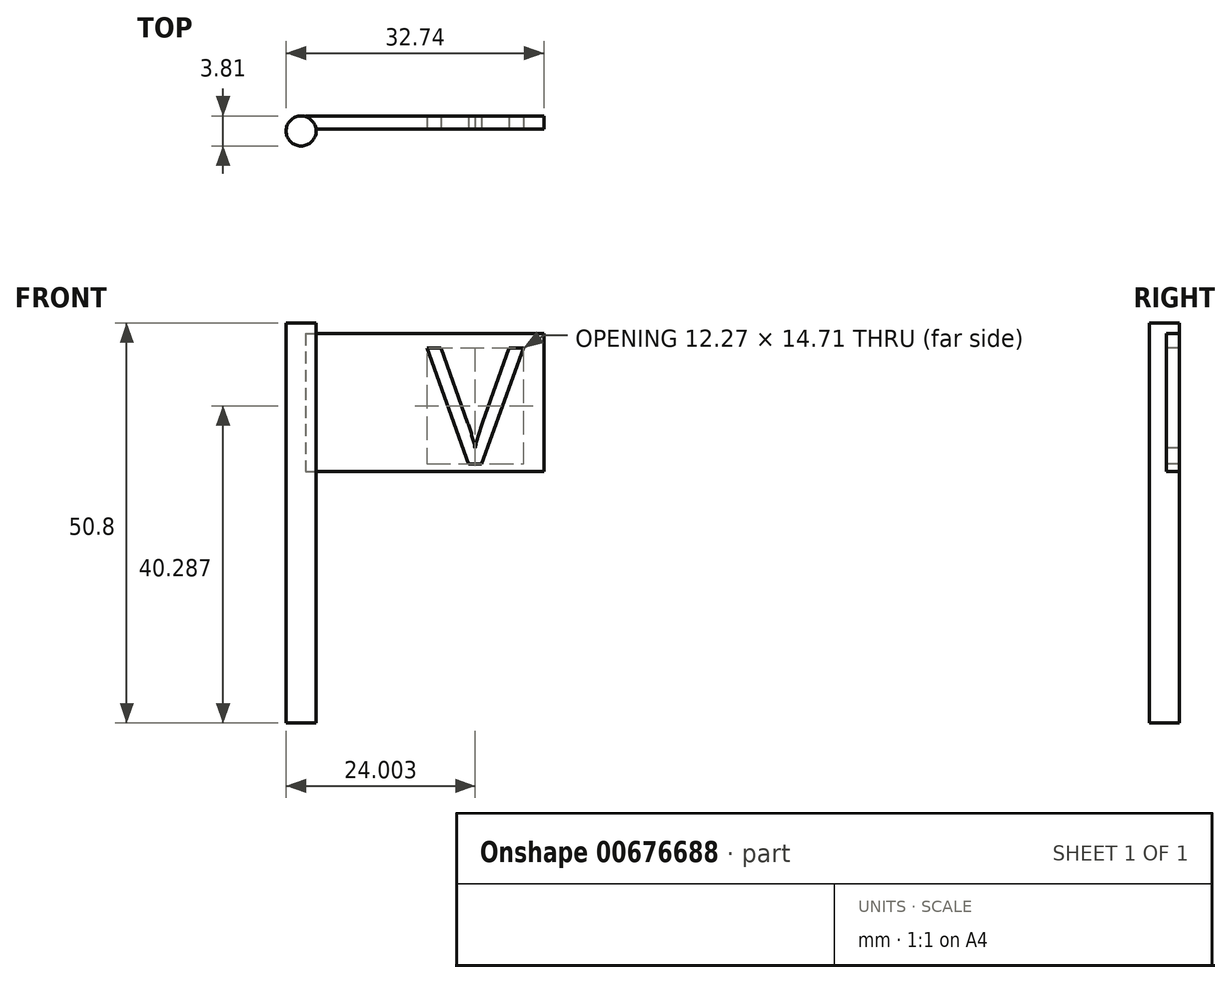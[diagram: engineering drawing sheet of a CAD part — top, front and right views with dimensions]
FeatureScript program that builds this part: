
annotation { "Feature Type Name" : "Feature", "Feature Type Description" : "" }
export const myFeature = defineFeature(function(context is Context, id is Id, definition is map)
    precondition{}
    {
        {
            var Q0;
            Q0=qCreatedBy(makeId("Top.planeOp"),FACE);
            var sketch = newSketch(context, id + "F0", { "sketchPlane" : qUnion([Q0])});
            skCircle(sketch, "E0", {"center": v(-29.57, 21.63) * mm, "radius": 1.9 * mm});
            skSolve(sketch);
        }
        {
            var Q0;
            Q0=makeQuery(id+"F0.imprint","IMPRINT",FACE,{"disambiguationData":[TD([[makeQuery(id+"F0.imprint","IMPRINT",EDGE,{"derivedFrom":sQuery(id+"F0.wireOp",EDGE,"E0")}),1.0]])]});
            extrude(context, id + "F1", {"entities" : qUnion([Q0]), "endBound" : BoundingType.SYMMETRIC, "depth" : 50.8 * mm, "offsetDistance" : 25.4 * mm});
        }
        {
            var Q0;
            Q0=qCreatedBy(makeId("Front.planeOp"),FACE);
            var sketch = newSketch(context, id + "F2", { "sketchPlane" : qUnion([Q0])});
            skLineSegment(sketch, "E1.bottom", {"start": v(-29.02, 24.05) * mm, "end": v(1.27, 24.05) * mm});
            skLineSegment(sketch, "E1.top", {"start": v(-29.02, 6.52) * mm, "end": v(1.27, 6.52) * mm});
            skLineSegment(sketch, "E1.left", {"start": v(-29.02, 24.05) * mm, "end": v(-29.02, 6.52) * mm});
            skLineSegment(sketch, "E1.right", {"start": v(1.27, 24.05) * mm, "end": v(1.27, 6.52) * mm});
            skText(sketch, "E2", { "text": "V", "fontName": "OpenSans-Regular.ttf"});
            const initialGuessF2  = {"E2": [-0.0136, 0.00753, 1, 0, 0.01484]};
            skSetInitialGuess(sketch, initialGuessF2);
            skSolve(sketch);
        }
        {
            var Q0;
            Q0=makeQuery(id+"F1.opExtrude","SWEPT_BODY",BODY,{"disambiguationData":[OSD([sQuery(id+"F0.wireOp",EDGE,"E0")])]});
            transform(context, id + "F3", {"entities" : qUnion([Q0]), "transformType" : TransformType.TRANSLATION_3D, "dx" : 0 * mm, "dy" : -21.84 * mm, "dz" : 0 * mm, "makeCopy" : false});
        }
        {
            var Q0;
            Q0=makeQuery(id+"F2.imprint","IMPRINT",FACE,{"disambiguationData":[TD([[makeQuery(id+"F2.imprint","IMPRINT",EDGE,{"derivedFrom":sQuery(id+"F2.wireOp",EDGE,"E1.bottom")}),-1.0]])]});
            extrude(context, id + "F4", {"entities" : qUnion([Q0]), "operationType" : NewBodyOperationType.ADD, "oppositeDirection" : true, "depth" : 1.69 * mm, "offsetDistance" : 25.4 * mm});
        }
    });
